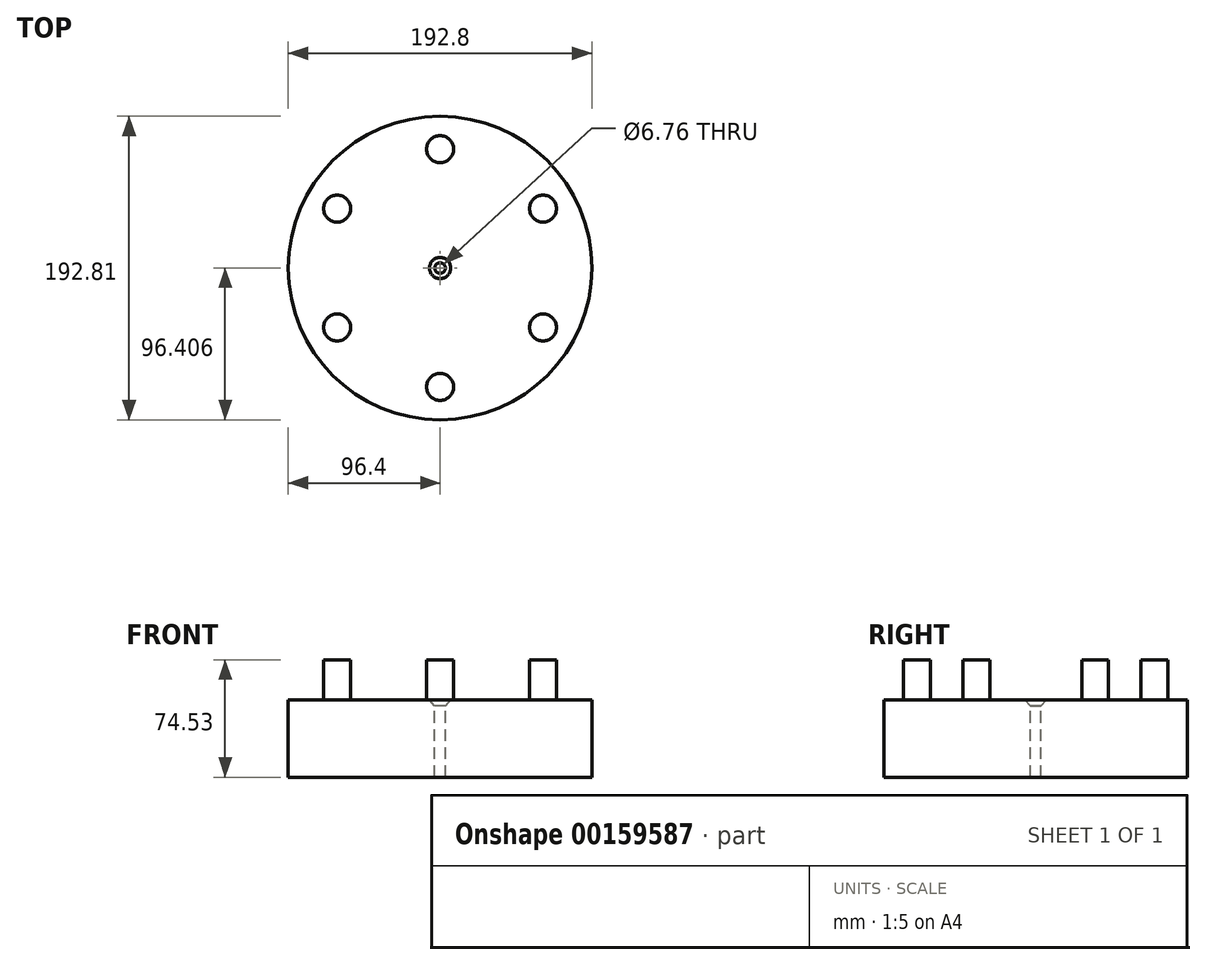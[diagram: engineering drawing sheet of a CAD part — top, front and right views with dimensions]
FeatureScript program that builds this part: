
annotation { "Feature Type Name" : "Feature", "Feature Type Description" : "" }
export const myFeature = defineFeature(function(context is Context, id is Id, definition is map)
    precondition{}
    {
        {
            var Q0;
            Q0=qCreatedBy(makeId("Right.planeOp"),FACE);
            var sketch = newSketch(context, id + "F0", { "sketchPlane" : qUnion([Q0])});
            skLineSegment(sketch, "E0.bottom", {"start": v(-46.78, 40.35) * mm, "end": v(49.62, 40.35) * mm});
            skLineSegment(sketch, "E0.top", {"start": v(-46.78, -8.78) * mm, "end": v(49.62, -8.78) * mm});
            skLineSegment(sketch, "E0.left", {"start": v(-46.78, 40.35) * mm, "end": v(-46.78, -8.78) * mm});
            skLineSegment(sketch, "E0.right", {"start": v(49.62, 40.35) * mm, "end": v(49.62, -8.78) * mm});
            skLineSegment(sketch, "E1", {"start": v(-379.78, 143.32) * mm, "end": v(-379.78, 0) * mm});
            skSolve(sketch);
        }
        {
            var Q0;
            Q0 = qSketchRegion(id + "F0", true);
            var Q1;
            Q1=sQuery(id+"F0.wireOp",EDGE,"E0.left");
            revolve(context, id + "F1", {"entities" : qUnion([Q0]), "axis" : qUnion([Q1]), "revolveType" : RevolveType.FULL});
        }
        {
            var Q0;
            Q0=makeQuery(id+"F1.opRevolve","SWEPT_FACE",FACE,{"disambiguationData":[OSD([sQuery(id+"F0.wireOp",EDGE,"E0.bottom")])]});
            extrude(context, id + "F2", {"entities" : qUnion([Q0]), "operationType" : NewBodyOperationType.ADD, "depth" : 25.4 * mm});
        }
        {
            var Q0;
            Q0=makeQuery(id+"F2.opExtrude","CAP_FACE",FACE,{"disambiguationData":[OSD([sQuery(id+"F0.wireOp",EDGE,"E0.bottom")])],"isStart":false});
            var sketch = newSketch(context, id + "F3", { "sketchPlane" : qUnion([Q0])});
            skCircle(sketch, "E2", {"center": v(0, -122.29) * mm, "radius": 8.56 * mm});
            skCircle(sketch, "E3.1.0", {"center": v(65.39, -84.54) * mm, "radius": 8.56 * mm});
            skCircle(sketch, "E3.2.0", {"center": v(65.39, -9.03) * mm, "radius": 8.56 * mm});
            skCircle(sketch, "E3.3.0", {"center": v(0, 28.72) * mm, "radius": 8.56 * mm});
            skCircle(sketch, "E3.4.0", {"center": v(-65.39, -9.03) * mm, "radius": 8.56 * mm});
            skCircle(sketch, "E3.5.0", {"center": v(-65.39, -84.54) * mm, "radius": 8.56 * mm});
            skPoint(sketch, "E3.center", {"position": v(0, -46.78) * mm});
            skSolve(sketch);
        }
        {
            var Q0;
            Q0=makeQuery(id+"F3.imprint","IMPRINT",FACE,{"disambiguationData":[TD([[makeQuery(id+"F3.imprint","IMPRINT",EDGE,{"derivedFrom":sQuery(id+"F3.wireOp",EDGE,"E2")}),-1.0]])]});
            extrude(context, id + "F4", {"entities" : qUnion([Q0]), "operationType" : NewBodyOperationType.REMOVE, "oppositeDirection" : true, "depth" : 25.4 * mm});
        }
        {
            var Q0;
            Q0=makeQuery(id+"F4.boolean.opBoolean","COPY",FACE,{"derivedFrom":makeQuery(id+"F4.opExtrude","CAP_FACE",FACE,{"disambiguationData":[OSD([sQuery(id+"F0.wireOp",EDGE,"E0.bottom"),sQuery(id+"F0.wireOp",EDGE,"E0.right"),sQuery(id+"F3.wireOp",EDGE,"E2"),sQuery(id+"F3.wireOp",EDGE,"E3.1.0"),sQuery(id+"F3.wireOp",EDGE,"E3.2.0"),sQuery(id+"F3.wireOp",EDGE,"E3.3.0"),sQuery(id+"F3.wireOp",EDGE,"E3.4.0"),sQuery(id+"F3.wireOp",EDGE,"E3.5.0")])],"isStart":false})});
            var sketch = newSketch(context, id + "F5", { "sketchPlane" : qUnion([Q0])});
            skPoint(sketch, "E4", {"position": v(0, -46.78) * mm});
            skSolve(sketch);
        }
        {
            var Q0;
            Q0=sQuery(id+"F5.wireOp",VERTEX,"E4");
            var Q1;
            Q1=makeQuery(id+"F1.opRevolve","SWEPT_BODY",BODY,{"disambiguationData":[OSD([sQuery(id+"F0.wireOp",EDGE,"E0.bottom"),sQuery(id+"F0.wireOp",EDGE,"E0.top"),sQuery(id+"F0.wireOp",EDGE,"E0.left"),sQuery(id+"F0.wireOp",EDGE,"E0.right")])]});
            hole(context, id + "F6", {"style" : HoleStyle.C_SINK, "endStyle" : HoleEndStyle.THROUGH, "standardTappedOrClearance" : lookupTablePath({ "standard" : "ANSI", "fit" : "Normal (ASME)", "size" : "1/4", "type" : "Clearance" }), "standardBlindInLast" : lookupTablePath({ "fit" : "Free", "standard" : "ANSI", "size" : "1/4", "type" : "Clearance" }), "holeDiameter" : 6.76 * mm, "cSinkDiameter" : 13.5 * mm, "cSinkAngle" : 82 * degree, "locations" : qUnion([Q0]), "scope" : qUnion([Q1]), "isTappedThrough" : true});
        }
    });
